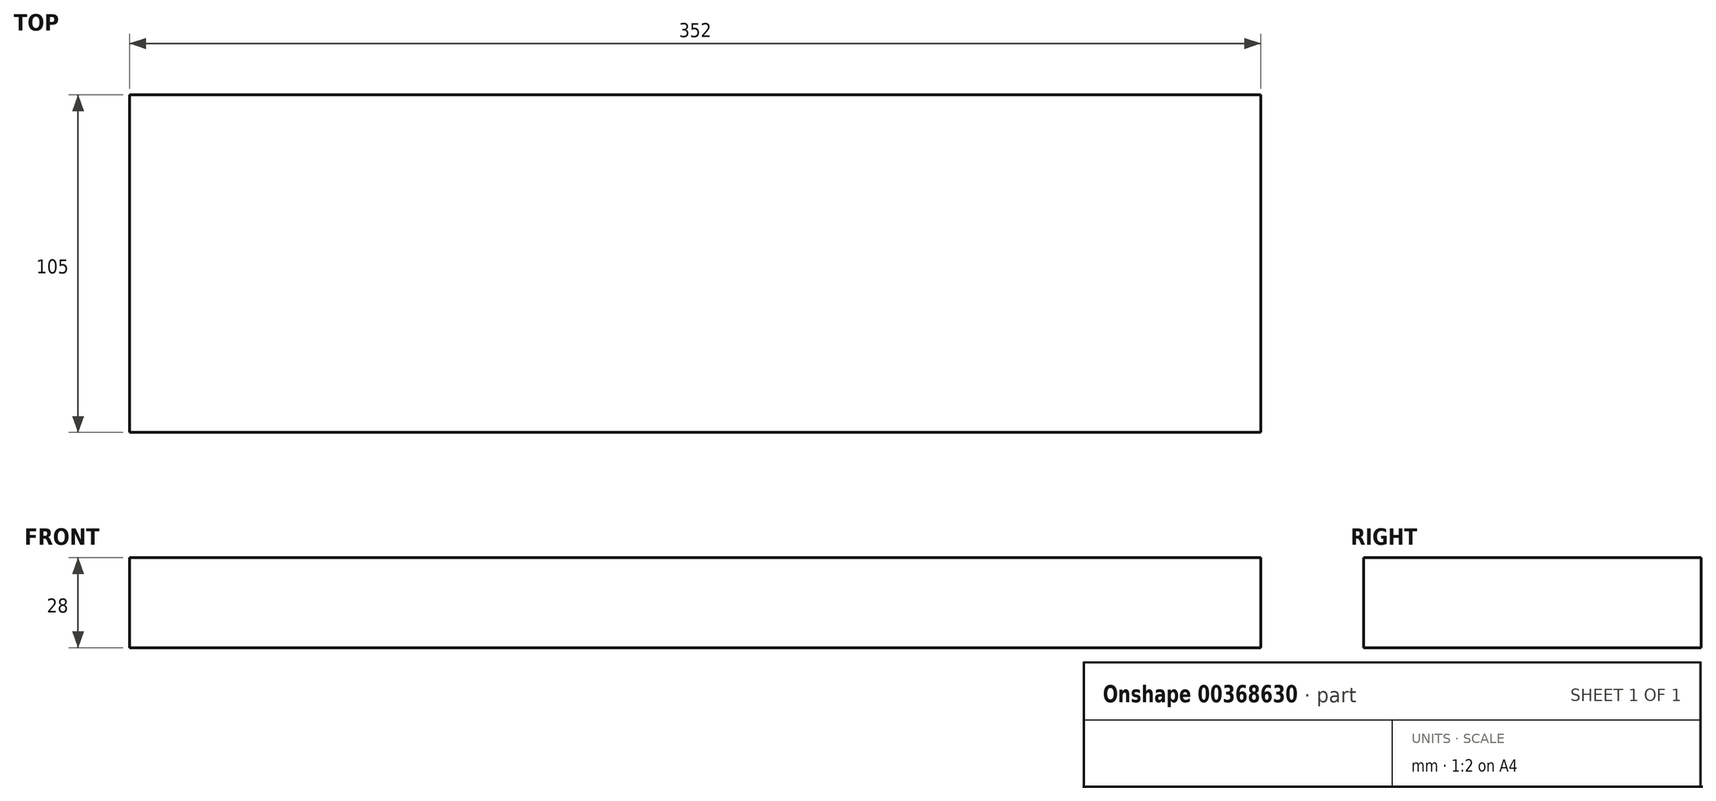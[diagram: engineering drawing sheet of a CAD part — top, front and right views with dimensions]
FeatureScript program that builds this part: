
annotation { "Feature Type Name" : "Feature", "Feature Type Description" : "" }
export const myFeature = defineFeature(function(context is Context, id is Id, definition is map)
    precondition{}
    {
        {
            var Q0;
            Q0=qCreatedBy(makeId("Top.planeOp"),FACE);
            var sketch = newSketch(context, id + "F0", { "sketchPlane" : qUnion([Q0])});
            skLineSegment(sketch, "E0.bottom", {"start": v(176, -52.5) * mm, "end": v(-176, -52.5) * mm});
            skLineSegment(sketch, "E0.top", {"start": v(176, 52.5) * mm, "end": v(-176, 52.5) * mm});
            skLineSegment(sketch, "E0.left", {"start": v(176, -52.5) * mm, "end": v(176, 52.5) * mm});
            skLineSegment(sketch, "E0.right", {"start": v(-176, -52.5) * mm, "end": v(-176, 52.5) * mm});
            skPoint(sketch, "E0.middle", {"position": v(0, 0) * mm});
            skSolve(sketch);
        }
        {
            var Q0;
            Q0=makeQuery(id+"F0.imprint","IMPRINT",FACE,{"disambiguationData":[TD([[makeQuery(id+"F0.imprint","IMPRINT",EDGE,{"derivedFrom":sQuery(id+"F0.wireOp",EDGE,"E0.bottom")}),-1.0]])]});
            extrude(context, id + "F1", {"entities" : qUnion([Q0]), "depth" : 28 * mm});
        }
    });
